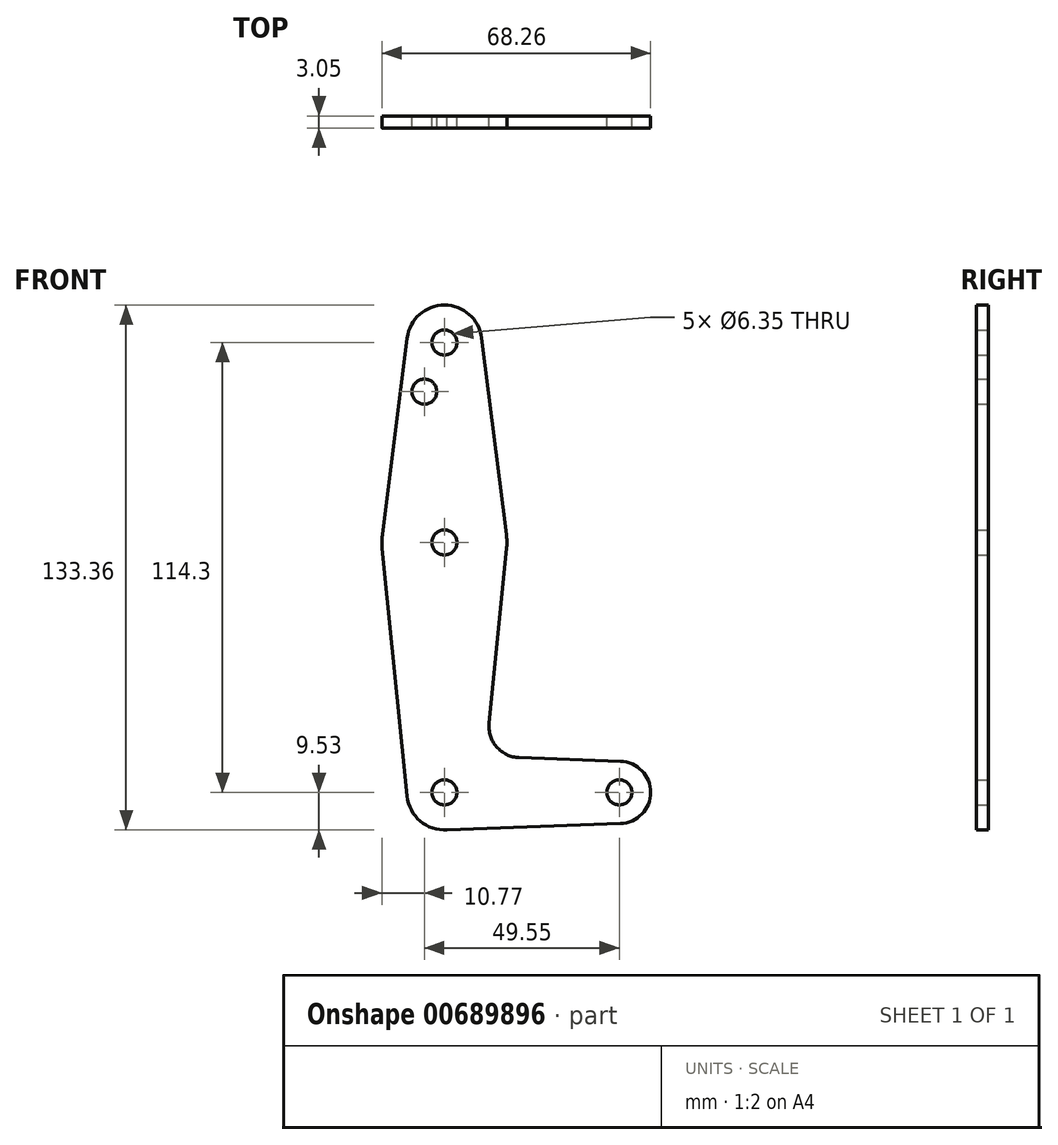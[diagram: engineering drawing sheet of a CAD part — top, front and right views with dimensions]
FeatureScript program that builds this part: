
annotation { "Feature Type Name" : "Feature", "Feature Type Description" : "" }
export const myFeature = defineFeature(function(context is Context, id is Id, definition is map)
    precondition{}
    {
        {
            var Q0;
            Q0=qCreatedBy(makeId("Front.planeOp"),FACE);
            var sketch = newSketch(context, id + "F0", { "sketchPlane" : qUnion([Q0])});
            skLineSegment(sketch, "E0", {"start": v(0, 0) * mm, "end": v(0, 63.5) * mm, "construction": true});
            skLineSegment(sketch, "E1", {"start": v(0, 63.5) * mm, "end": v(0, 114.3) * mm, "construction": true});
            skLineSegment(sketch, "E2", {"start": v(0, 0) * mm, "end": v(44.45, 0) * mm, "construction": true});
            skCircle(sketch, "E3", {"center": v(0, 114.3) * mm, "radius": 9.53 * mm});
            skCircle(sketch, "E4", {"center": v(0, 63.5) * mm, "radius": 15.88 * mm});
            skCircle(sketch, "E5", {"center": v(0, 0) * mm, "radius": 9.53 * mm});
            skCircle(sketch, "E6", {"center": v(44.45, 0) * mm, "radius": 7.94 * mm});
            skLineSegment(sketch, "E7", {"start": v(-9.45, 115.5) * mm, "end": v(-15.75, 65.48) * mm});
            skLineSegment(sketch, "E8", {"start": v(9.45, 115.5) * mm, "end": v(15.75, 65.48) * mm});
            skLineSegment(sketch, "E9", {"start": v(18.97, 8.85) * mm, "end": v(44.73, 7.93) * mm});
            skLineSegment(sketch, "E10", {"start": v(0, -9.53) * mm, "end": v(44.73, -7.93) * mm});
            skLineSegment(sketch, "E11", {"start": v(-15.8, 61.91) * mm, "end": v(-9.48, -0.95) * mm});
            skLineSegment(sketch, "E12", {"start": v(11.34, 17.59) * mm, "end": v(15.8, 61.91) * mm});
            skCircle(sketch, "E13", {"center": v(0, 114.3) * mm, "radius": 3.18 * mm});
            skCircle(sketch, "E14", {"center": v(-5.1, 101.82) * mm, "radius": 3.18 * mm});
            skCircle(sketch, "E15", {"center": v(0, 63.5) * mm, "radius": 3.18 * mm});
            skCircle(sketch, "E16", {"center": v(0, 0) * mm, "radius": 3.18 * mm});
            skCircle(sketch, "E17", {"center": v(44.45, 0) * mm, "radius": 3.18 * mm});
            skPoint(sketch, "E18.newPointB", {"position": v(0, 9.53) * mm});
            skArc(sketch, "E18.filletArc", {"start": v(11.34, 17.59) * mm, "mid": v(13.26, 11.57) * mm, "end": v(18.97, 8.85) * mm});
            skSolve(sketch);
        }
        {
            var Q0;
            Q0 = qSketchRegion(id + "F0", true);
            extrude(context, id + "F1", {"entities" : qUnion([Q0]), "depth" : 3.05 * mm, "offsetDistance" : 25.4 * mm});
        }
    });
